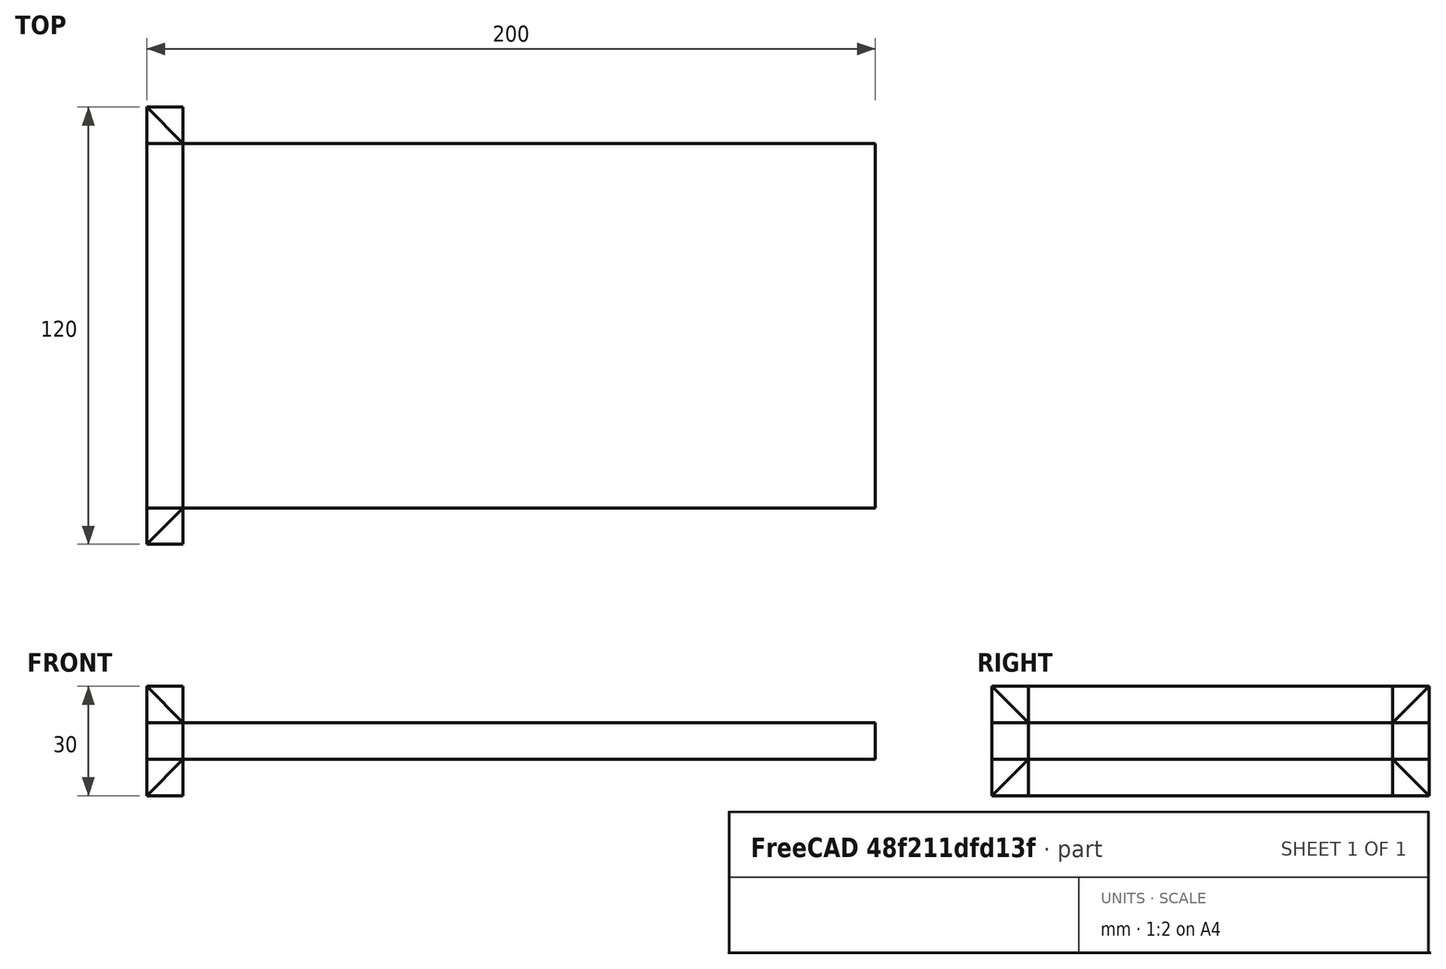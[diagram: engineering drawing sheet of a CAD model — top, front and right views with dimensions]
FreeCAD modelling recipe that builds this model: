
FCSTD DOCUMENT  (FreeCAD 0.21R33694 (Git))
Label: Cruciform Fillet Test
License: All rights reserved
LicenseURL: http://en.wikipedia.org/wiki/All_rights_reserved
objects: Part::Feature×8, Sketcher::SketchObject×4, Part::Extrusion×4, Part::FeaturePython×2, Part::Box×1, App::MaterialObjectPython×1, Fem::FemSolverObjectPython×1, Fem::ConstraintFixed×1, Fem::ConstraintPressure×1, Fem::FeaturePython×1, Fem::FemMeshObjectPython×1, Fem::FemAnalysis×1
note: 19 computed .brp shape members not serialized (recipe doc carries the construction recipe); baked Part::Feature solids carry a one-line shape summary decoded from their .brp

FEATURE [Part::Box] Box  label="plate"
  AttacherType = Attacher::AttachEngine3D
  Height = 10
  Length = 200
  Width = 100
FEATURE [Sketcher::SketchObject] Sketch
  FullyConstrained = true
  MapMode = 5
  Placement = pos=(0,0,0) rot=(1,0,0;1.5708rad)
  Support = -> [Box]
  sketch-geometry (6):
    g0: LineSegment StartX=0 StartY=10 StartZ=0 EndX=10 EndY=10 EndZ=0
    g1: LineSegment StartX=10 StartY=10 StartZ=0 EndX=0 EndY=20 EndZ=0
    g2: LineSegment StartX=0 StartY=20 StartZ=0 EndX=0 EndY=10 EndZ=0
    g3: LineSegment StartX=0 StartY=0 StartZ=0 EndX=10 EndY=0 EndZ=0
    g4: LineSegment StartX=10 StartY=0 StartZ=0 EndX=0 EndY=-10 EndZ=0
    g5: LineSegment StartX=0 StartY=-10 StartZ=0 EndX=0 EndY=0 EndZ=0
  constraints (17):
    c: Horizontal(g0)
    c: Coincident(g0,g1)
    c: Coincident(g1,g2)
    c: Coincident(g2,g0)
    c: DistanceY(g-1,g0) = 10
    c: Vertical(g2)
    c: DistanceX(g0,g0) = 10
    c: DistanceY(g2,g2) = 10
    c: DistanceX(g-1,g0) = 0
    c: Coincident(g3,g4)
    c: Coincident(g4,g5)
    c: Coincident(g5,g3)
    c: Coincident(g3,g-1)
    c: Vertical(g5)
    c: Horizontal(g3)
    c: DistanceX(g3,g3) = 10
    c: DistanceY(g5,g5) = 10
FEATURE [Part::Extrusion] Extrude
  Base = -> Sketch
  Dir = (0,-1,2e-16)
  DirMode = 2
  FaceMakerClass = Part::FaceMakerBullseye
  LengthFwd = -110
  LengthRev = -10
  Solid = true
  Symmetric = false
FEATURE [App::MaterialObjectPython] MaterialSolid  # material (typed FeaturePython)
  Category = 0
  Material = AuthorAndLicense=(c) 2014 M. Münch - GNU Lesser General Public License (LGPL),CardName=Steel-St-E-315,Density=7800 kg/m^3,Father=Metal,+13 more (map truncated)
FEATURE [Fem::FemSolverObjectPython] SolverCcxTools  # FEM object (typed FeaturePython)
  AnalysisType = 0
  BeamShellResultOutput3D = false
  BucklingFactors = 1
  EigenmodeHighLimit = 1000000
  EigenmodeLowLimit = 0
  EigenmodesCount = 10
  GeometricalNonlinearity = 0
  IterationsControlParameterCutb = 0.25,0.5,0.75,0.85,,,1.5,
  IterationsControlParameterIter = 4,8,9,200,10,400,,200,,
  IterationsControlParameterTimeUse = false
  IterationsThermoMechMaximum = 2000
  IterationsUserDefinedIncrementations = false
  IterationsUserDefinedTimeStepLength = false
  MaterialNonlinearity = 0
  MatrixSolverType = 0
  SplitInputWriter = false
  ThermoMechSteadyState = true
  TimeEnd = 1
  TimeInitialStep = 0.01
FEATURE [Sketcher::SketchObject] Sketch001
  FullyConstrained = true
  MapMode = 5
  Placement = pos=(0,0,0) rot=(1,0,0;3.14159rad)
  Support = -> [Box]
  sketch-geometry (6):
    g0: LineSegment StartX=0 StartY=10 StartZ=0 EndX=10 EndY=0 EndZ=0
    g1: LineSegment StartX=10 StartY=0 StartZ=0 EndX=0 EndY=0 EndZ=0
    g2: LineSegment StartX=0 StartY=0 StartZ=0 EndX=0 EndY=10 EndZ=0
    g3: LineSegment StartX=0 StartY=-100 StartZ=0 EndX=10 EndY=-100 EndZ=0
    g4: LineSegment StartX=10 StartY=-100 StartZ=0 EndX=0 EndY=-110 EndZ=0
    g5: LineSegment StartX=0 StartY=-110 StartZ=0 EndX=0 EndY=-100 EndZ=0
  constraints (17):
    c: Coincident(g0,g1)
    c: Coincident(g1,g2)
    c: Coincident(g2,g0)
    c: Horizontal(g3)
    c: Coincident(g3,g4)
    c: Coincident(g4,g5)
    c: Coincident(g5,g3)
    c: Coincident(g1,g-1)
    c: Vertical(g2)
    c: Horizontal(g1)
    c: DistanceX(g1,g1) = 10
    c: DistanceY(g2,g2) = 10
    c: DistanceY(g3,g1) = 100
    c: DistanceY(g4,g1) = 110
    c: Vertical(g5)
    c: DistanceX(g1,g3) = 0
    c: DistanceX(g3,g3) = 10
FEATURE [Part::Extrusion] Extrude001
  Base = -> Sketch001
  Dir = (0,0,-1)
  DirMode = 2
  FaceMakerClass = Part::FaceMakerBullseye
  LengthFwd = 10
  LengthRev = 20
  Solid = true
  Symmetric = false
FEATURE [Part::FeaturePython] BooleanFragments  # WARN: FeaturePython — macro-defined, semantics opaque (R4)
  Mode = 0
  Objects = -> [Extrude,Extrude001]
  Tolerance = 0
FEATURE [Sketcher::SketchObject] Sketch002
  FullyConstrained = true
  MapMode = 5
  Placement = pos=(0,0,0) rot=(1,0,0;1.5708rad)
  sketch-geometry (6):
    g0: LineSegment StartX=0 StartY=10 StartZ=0 EndX=10 EndY=10 EndZ=0
    g1: LineSegment StartX=10 StartY=10 StartZ=0 EndX=0 EndY=20 EndZ=0
    g2: LineSegment StartX=0 StartY=20 StartZ=0 EndX=0 EndY=10 EndZ=0
    g3: LineSegment StartX=0 StartY=0 StartZ=0 EndX=10 EndY=0 EndZ=0
    g4: LineSegment StartX=10 StartY=0 StartZ=0 EndX=0 EndY=-10 EndZ=0
    g5: LineSegment StartX=0 StartY=-10 StartZ=0 EndX=0 EndY=0 EndZ=0
  constraints (17):
    c: Horizontal(g0)
    c: Coincident(g0,g1)
    c: Coincident(g1,g2)
    c: Coincident(g2,g0)
    c: DistanceY(g-1,g0) = 10
    c: Vertical(g2)
    c: DistanceX(g0,g0) = 10
    c: DistanceY(g2,g2) = 10
    c: DistanceX(g-1,g0) = 0
    c: Coincident(g3,g4)
    c: Coincident(g4,g5)
    c: Coincident(g5,g3)
    c: Coincident(g3,g-1)
    c: Vertical(g5)
    c: Horizontal(g3)
    c: DistanceX(g3,g3) = 10
    c: DistanceY(g5,g5) = 10
FEATURE [Part::Extrusion] Extrude002
  Base = -> Sketch002
  Dir = (0,-1,2e-16)
  DirMode = 2
  FaceMakerClass = Part::FaceMakerBullseye
  LengthFwd = -110
  LengthRev = -10
  Solid = true
  Symmetric = false
FEATURE [Sketcher::SketchObject] Sketch003
  FullyConstrained = true
  MapMode = 5
  Placement = pos=(0,0,0) rot=(1,0,0;3.14159rad)
  sketch-geometry (6):
    g0: LineSegment StartX=0 StartY=10 StartZ=0 EndX=10 EndY=0 EndZ=0
    g1: LineSegment StartX=10 StartY=0 StartZ=0 EndX=0 EndY=0 EndZ=0
    g2: LineSegment StartX=0 StartY=0 StartZ=0 EndX=0 EndY=10 EndZ=0
    g3: LineSegment StartX=0 StartY=-100 StartZ=0 EndX=10 EndY=-100 EndZ=0
    g4: LineSegment StartX=10 StartY=-100 StartZ=0 EndX=0 EndY=-110 EndZ=0
    g5: LineSegment StartX=0 StartY=-110 StartZ=0 EndX=0 EndY=-100 EndZ=0
  constraints (17):
    c: Coincident(g0,g1)
    c: Coincident(g1,g2)
    c: Coincident(g2,g0)
    c: Horizontal(g3)
    c: Coincident(g3,g4)
    c: Coincident(g4,g5)
    c: Coincident(g5,g3)
    c: Coincident(g1,g-1)
    c: Vertical(g2)
    c: Horizontal(g1)
    c: DistanceX(g1,g1) = 10
    c: DistanceY(g2,g2) = 10
    c: DistanceY(g3,g1) = 100
    c: DistanceY(g4,g1) = 110
    c: Vertical(g5)
    c: DistanceX(g1,g3) = 0
    c: DistanceX(g3,g3) = 10
FEATURE [Part::Extrusion] Extrude003
  Base = -> Sketch003
  Dir = (0,0,-1)
  DirMode = 2
  FaceMakerClass = Part::FaceMakerBullseye
  LengthFwd = 10
  LengthRev = 20
  Solid = true
  Symmetric = false
FEATURE [Part::Feature] Solid
  shape: bbox 10 x 10 x 10 mm, 5 faces (baked)
FEATURE [Part::Feature] Solid002
  shape: bbox 10 x 100 x 10 mm, 5 faces (baked)
FEATURE [Part::Feature] Solid003
  shape: bbox 10 x 10 x 10 mm, 5 faces (baked)
FEATURE [Part::Feature] Solid005
  shape: bbox 10 x 10 x 10 mm, 5 faces (baked)
FEATURE [Part::Feature] Solid007
  shape: bbox 10 x 100 x 10 mm, 5 faces (baked)
FEATURE [Part::Feature] Solid008
  shape: bbox 10 x 10 x 10 mm, 5 faces (baked)
FEATURE [Part::Feature] Solid011
  shape: bbox 10 x 10 x 10 mm, 5 faces (baked)
FEATURE [Part::Feature] Solid014
  shape: bbox 10 x 10 x 10 mm, 5 faces (baked)
FEATURE [Part::FeaturePython] BooleanFragments001  # WARN: FeaturePython — macro-defined, semantics opaque (R4)
  Mode = 2
  Objects = -> [Box,Solid,Solid002,Solid003,Solid005,Solid007,Solid008,Solid011,Solid014]
  Tolerance = 0
FEATURE [Fem::ConstraintFixed] ConstraintFixed
  NormalDirection = (-1,0,0)
  Normals = (78) [(-1,0,0),(-1,0,0),(-1,0,0),(-1,0,0),(-1,0,0),(-1,0,0),(-1,0,0),(-1,0,0),(-1,0,0),(-1,0,0),(-1,0,0),(-1,0,0),(-1,0,0),(-1,0,0),(-1,0,0),(-1,0,0),+62 more]
  Points = (78) [(0,1.77636e-15,20),(0,0,15),(0,0,10),(0,-5,20),(0,-5,15),(0,-5,10),(0,-10,20),(0,-10,15),(0,-10,10),(0,0,0),(0,-5,0),(0,-10,0),(0,0,5),(0,-5,5),+64 more]
  References = -> [BooleanFragments001]
FEATURE [Fem::ConstraintPressure] ConstraintPressure
  NormalDirection = (1,0,0)
  Normals = (12) [(1,0,0),(1,0,0),(1,0,0),(1,0,0),(1,0,0),(1,0,0),(1,0,0),(1,0,0),(1,0,0),(1,0,0),(1,0,0),(1,0,0)]
  Points = (12) [(200,100,0),(200,100,5),(200,100,10),(200,66.6667,0),(200,66.6667,5),(200,66.6667,10),(200,33.3333,0),(200,33.3333,5),(200,33.3333,10),(200,0,0),+2 more]
  Pressure = 100
  References = -> [BooleanFragments001]
  Reversed = true
FEATURE [Fem::FeaturePython] MeshRegion  # FEM object (typed FeaturePython)
  CharacteristicLength = 2
  References = -> [BooleanFragments001]
FEATURE [Fem::FemMeshObjectPython] FEMMeshGmsh  # FEM object (typed FeaturePython)
  Algorithm2D = 0
  Algorithm3D = 0
  CharacteristicLengthMax = 5
  CharacteristicLengthMin = 0
  CoherenceMesh = true
  ElementDimension = 0
  ElementOrder = 1
  GeometryTolerance = 1e-06
  GroupsOfNodes = false
  HighOrderOptimize = 0
  MeshRegionList = -> [MeshRegion]
  MeshSizeFromCurvature = 12
  OptimizeNetgen = false
  OptimizeStd = true
  Part = -> BooleanFragments001
  RecombinationAlgorithm = 0
  Recombine3DAll = false
  RecombineAll = false
  SecondOrderLinear = false
FEATURE [Fem::FemAnalysis] Analysis
  Group = -> [ConstraintFixed,ConstraintPressure,MaterialSolid,SolverCcxTools,FEMMeshGmsh]
